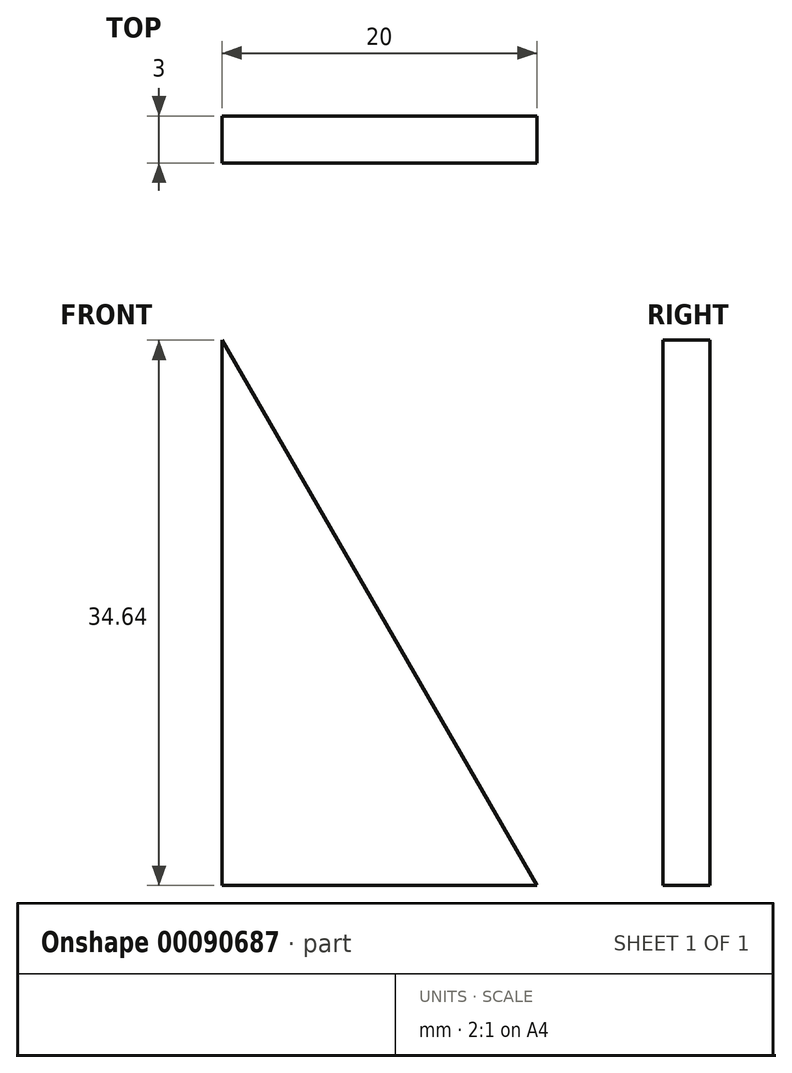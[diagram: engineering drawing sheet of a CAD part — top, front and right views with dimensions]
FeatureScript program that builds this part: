
annotation { "Feature Type Name" : "Feature", "Feature Type Description" : "" }
export const myFeature = defineFeature(function(context is Context, id is Id, definition is map)
    precondition{}
    {
        {
            var Q0;
            Q0=qCreatedBy(makeId("Front.planeOp"),FACE);
            var sketch = newSketch(context, id + "F0", { "sketchPlane" : qUnion([Q0])});
            skLineSegment(sketch, "E0", {"start": v(0, 0) * mm, "end": v(20, 0) * mm});
            skLineSegment(sketch, "E1", {"start": v(20, 0) * mm, "end": v(0, 34.64) * mm});
            skLineSegment(sketch, "E2", {"start": v(0, 34.64) * mm, "end": v(0, 0) * mm});
            skSolve(sketch);
        }
        {
            var Q0;
            Q0 = qSketchRegion(id + "F0", true);
            extrude(context, id + "F1", {"entities" : qUnion([Q0]), "depth" : 3 * mm});
        }
        {
            var Q0;
            Q0=makeQuery(id+"F1.opExtrude","SWEPT_BODY",BODY,{"disambiguationData":[OSD([sQuery(id+"F0.wireOp",EDGE,"E0"),sQuery(id+"F0.wireOp",EDGE,"E1"),sQuery(id+"F0.wireOp",EDGE,"E2")])]});
            var Q1;
            Q1=qCreatedBy(makeId("Front.planeOp"),FACE);
            transform(context, id + "F2", {"entities" : qUnion([Q0]), "transformType" : TransformType.TRANSLATION_DISTANCE, "transformDirection" : qUnion([Q1]), "distance" : 25.4 * mm, "makeCopy" : false});
        }
    });
